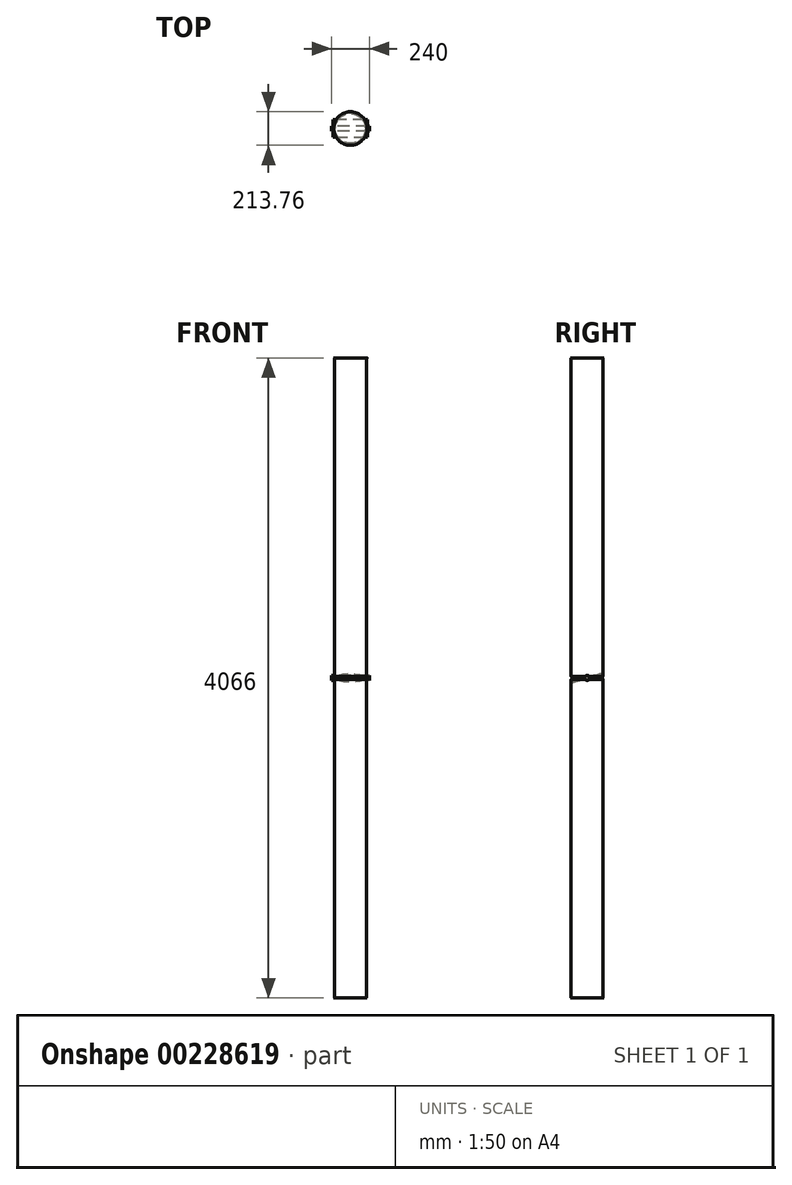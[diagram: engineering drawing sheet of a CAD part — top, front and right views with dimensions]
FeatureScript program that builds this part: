
annotation { "Feature Type Name" : "Feature", "Feature Type Description" : "" }
export const myFeature = defineFeature(function(context is Context, id is Id, definition is map)
    precondition{}
    {
        {
            var Q0;
            Q0=qCreatedBy(makeId("Top.planeOp"),FACE);
            var sketch = newSketch(context, id + "F0", { "sketchPlane" : qUnion([Q0])});
            skCircle(sketch, "E0", {"center": v(0, 0) * mm, "radius": 98 * mm});
            skSolve(sketch);
        }
        {
            var Q0;
            Q0=qSketchRegion(id+"F0",true);
            var Q1;
            Q1=sQuery(id+"F0.wireOp",EDGE,"E0");
            extrude(context, id + "F1", {"entities" : qUnion([Q0]), "surfaceEntities" : qUnion([Q1]), "endBound" : BoundingType.SYMMETRIC, "depth" : 6 * mm});
        }
        {
            var Q0;
            Q0=qCreatedBy(makeId("Top.planeOp"),FACE);
            var sketch = newSketch(context, id + "F2", { "sketchPlane" : qUnion([Q0])});
            skLineSegment(sketch, "E1", {"start": v(-75.72, 0) * mm, "end": v(75.22, 0) * mm});
            skSolve(sketch);
        }
        {
            var Q0;
            Q0=makeQuery(id+"F1.opExtrude","CAP_EDGE",EDGE,{"disambiguationData":[OSD([sQuery(id+"F0.wireOp",EDGE,"E0")])],"isStart":true});
            var Q1;
            Q1=makeQuery(id+"F1.opExtrude","CAP_EDGE",EDGE,{"disambiguationData":[OSD([sQuery(id+"F0.wireOp",EDGE,"E0")])],"isStart":false});
            fillet(context, id + "F3", {"entities" : qUnion([Q0, Q1]), "radius" : 3 * mm, "tangentPropagation" : true, "allowEdgeOverflow" : false});
        }
        {
            var Q0;
            Q0=qCreatedBy(makeId("Top.planeOp"),FACE);
            var sketch = newSketch(context, id + "F4", { "sketchPlane" : qUnion([Q0])});
            skCircle(sketch, "E2", {"center": v(0, 0) * mm, "radius": 101.6 * mm});
            skSolve(sketch);
        }
        {
            var Q0;
            Q0=qSketchRegion(id+"F4",true);
            extrude(context, id + "F5", {"entities" : qUnion([Q0]), "depth" : 2032 * mm, "hasSecondDirection" : true, "secondDirectionOppositeDirection" : true, "secondDirectionDepth" : 2032 * mm});
        }
        {
            var Q0;
            Q0=qCreatedBy(makeId("Right.planeOp"),FACE);
            var sketch = newSketch(context, id + "F6", { "sketchPlane" : qUnion([Q0])});
            skCircle(sketch, "E3", {"center": v(0, 0) * mm, "radius": 16 * mm});
            skSolve(sketch);
        }
        {
            var Q0;
            Q0=qSketchRegion(id+"F6",true);
            extrude(context, id + "F7", {"entities" : qUnion([Q0]), "endBound" : BoundingType.SYMMETRIC, "depth" : 240 * mm});
        }
        {
            var Q0;
            Q0=makeQuery(id+"F4.imprint","IMPRINT",FACE,{"disambiguationData":[TD([[makeQuery(id+"F4.imprint","IMPRINT",EDGE,{"derivedFrom":sQuery(id+"F4.wireOp",EDGE,"E2")}),1.0]])]});
            var Q1;
            Q1=sQuery(id+"F4.wireOp",EDGE,"E2");
            extrude(context, id + "F8", {"entities" : qUnion([Q0]), "surfaceEntities" : qUnion([Q1]), "endBound" : BoundingType.SYMMETRIC, "depth" : 17.2 * mm});
        }
        {
            var Q0;
            Q0=makeQuery(id+"F0.imprint","IMPRINT",FACE,{"disambiguationData":[TD([[makeQuery(id+"F0.imprint","IMPRINT",EDGE,{"derivedFrom":sQuery(id+"F0.wireOp",EDGE,"E0")}),1.0]])]});
            var Q1;
            Q1=sQuery(id+"F0.wireOp",EDGE,"E0");
            extrude(context, id + "F9", {"entities" : qUnion([Q0]), "surfaceEntities" : qUnion([Q1]), "endBound" : BoundingType.SYMMETRIC, "depth" : 50 * mm});
        }
        {
            var Q0;
            Q0=makeQuery(id+"F9.opExtrude","SWEPT_BODY",BODY,{"disambiguationData":[OSD([sQuery(id+"F0.wireOp",EDGE,"E0")])]});
            var Q1;
            Q1=makeQuery(id+"F8.opExtrude","SWEPT_BODY",BODY,{"disambiguationData":[OSD([sQuery(id+"F4.wireOp",EDGE,"E2")])]});
            booleanBodies(context, id + "F10", {"operationType" : BooleanOperationType.SUBTRACTION, "tools" : qUnion([Q0]), "targets" : qUnion([Q1])});
        }
        {
            var Q0;
            Q0=makeQuery(id+"F8.opExtrude","SWEPT_BODY",BODY,{"disambiguationData":[OSD([sQuery(id+"F4.wireOp",EDGE,"E2")])]});
            var Q1;
            Q1=makeQuery(id+"F5.opExtrude","SWEPT_BODY",BODY,{"disambiguationData":[OSD([sQuery(id+"F4.wireOp",EDGE,"E2")])]});
            booleanBodies(context, id + "F11", {"operationType" : BooleanOperationType.SUBTRACTION, "tools" : qUnion([Q0]), "targets" : qUnion([Q1])});
        }
        {
            var Q0;
            Q0=makeQuery(id+"F11.opBoolean","COPY",EDGE,{"derivedFrom":makeQuery(id+"F8.opExtrude","CAP_EDGE",EDGE,{"disambiguationData":[OSD([sQuery(id+"F4.wireOp",EDGE,"E2")])],"isStart":true})});
            var Q1;
            Q1=makeQuery(id+"F11.opBoolean","COPY",EDGE,{"derivedFrom":makeQuery(id+"F10.opBoolean","INTERSECT",EDGE,{"derivedFrom":[makeQuery(id+"F8.opExtrude","CAP_FACE",FACE,{"disambiguationData":[OSD([sQuery(id+"F4.wireOp",EDGE,"E2")])],"isStart":true}),makeQuery(id+"F9.opExtrude","SWEPT_FACE",FACE,{"disambiguationData":[OSD([sQuery(id+"F0.wireOp",EDGE,"E0")])]})]})});
            var Q2;
            Q2=makeQuery(id+"F11.opBoolean","COPY",EDGE,{"derivedFrom":makeQuery(id+"F10.opBoolean","INTERSECT",EDGE,{"derivedFrom":[makeQuery(id+"F8.opExtrude","CAP_FACE",FACE,{"disambiguationData":[OSD([sQuery(id+"F4.wireOp",EDGE,"E2")])],"isStart":false}),makeQuery(id+"F9.opExtrude","SWEPT_FACE",FACE,{"disambiguationData":[OSD([sQuery(id+"F0.wireOp",EDGE,"E0")])]})]})});
            var Q3;
            Q3=makeQuery(id+"F11.opBoolean","COPY",EDGE,{"derivedFrom":makeQuery(id+"F8.opExtrude","CAP_EDGE",EDGE,{"disambiguationData":[OSD([sQuery(id+"F4.wireOp",EDGE,"E2")])],"isStart":false})});
            fillet(context, id + "F12", {"entities" : qUnion([Q0, Q1, Q2, Q3]), "radius" : 1.5 * mm, "tangentPropagation" : true, "allowEdgeOverflow" : false});
        }
        {
            var Q0;
            Q0=qCreatedBy(makeId("Top.planeOp"),FACE);
            var sketch = newSketch(context, id + "F13", { "sketchPlane" : qUnion([Q0])});
            skLineSegment(sketch, "E4.bottom", {"start": v(-110.32, -54.73) * mm, "end": v(109.68, -54.73) * mm});
            skLineSegment(sketch, "E4.top", {"start": v(-110.32, 55.27) * mm, "end": v(109.68, 55.27) * mm});
            skLineSegment(sketch, "E4.left", {"start": v(-110.32, -54.73) * mm, "end": v(-110.32, 55.27) * mm});
            skLineSegment(sketch, "E4.right", {"start": v(109.68, -54.73) * mm, "end": v(109.68, 55.27) * mm});
            skSolve(sketch);
        }
        {
            var Q0;
            Q0=qSketchRegion(id+"F13",true);
            extrude(context, id + "F14", {"entities" : qUnion([Q0]), "endBound" : BoundingType.SYMMETRIC, "depth" : 6 * mm});
        }
        {
            var Q0;
            Q0=makeQuery(id+"F14.opExtrude","CAP_EDGE",EDGE,{"disambiguationData":[OSD([sQuery(id+"F13.wireOp",EDGE,"E4.bottom")])],"isStart":true});
            var Q1;
            Q1=makeQuery(id+"F14.opExtrude","CAP_EDGE",EDGE,{"disambiguationData":[OSD([sQuery(id+"F13.wireOp",EDGE,"E4.bottom")])],"isStart":false});
            var Q2;
            Q2=makeQuery(id+"F14.opExtrude","CAP_EDGE",EDGE,{"disambiguationData":[OSD([sQuery(id+"F13.wireOp",EDGE,"E4.top")])],"isStart":true});
            var Q3;
            Q3=makeQuery(id+"F14.opExtrude","CAP_EDGE",EDGE,{"disambiguationData":[OSD([sQuery(id+"F13.wireOp",EDGE,"E4.top")])],"isStart":false});
            fillet(context, id + "F15", {"entities" : qUnion([Q0, Q1, Q2, Q3]), "radius" : 3 * mm, "tangentPropagation" : true, "allowEdgeOverflow" : false});
        }
        {
            var Q0;
            Q0=makeQuery(id+"F1.opExtrude","SWEPT_BODY",BODY,{"disambiguationData":[OSD([sQuery(id+"F0.wireOp",EDGE,"E0")])]});
            var Q1;
            Q1=sQuery(id+"F2.wireOp",EDGE,"E1");
            transform(context, id + "F16", {"entities" : qUnion([Q0]), "transformType" : TransformType.ROTATION, "transformAxis" : qUnion([Q1]), "angle" : 15 * degree, "makeCopy" : false});
        }
        {
            var Q0;
            Q0=makeQuery(id+"F5.opExtrude","CAP_FACE",FACE,{"disambiguationData":[OSD([sQuery(id+"F4.wireOp",EDGE,"E2")])],"isStart":true});
            var sketch = newSketch(context, id + "F17", { "sketchPlane" : qUnion([Q0])});
            skCircle(sketch, "E5", {"center": v(0, 0) * mm, "radius": 106.52 * mm});
            skSolve(sketch);
        }
        {
            var Q0;
            Q0=makeQuery(id+"F17.imprint","IMPRINT",FACE,{"disambiguationData":[TD([[makeQuery(id+"F17.imprint","IMPRINT",EDGE,{"derivedFrom":makeQuery(id+"F5.opExtrude","CAP_EDGE",EDGE,{"disambiguationData":[OSD([sQuery(id+"F4.wireOp",EDGE,"E2")])],"isStart":true})}),-1.0]])]});
            var Q1;
            Q1=makeQuery(id+"F17.imprint","IMPRINT",FACE,{"disambiguationData":[TD([[makeQuery(id+"F17.imprint","IMPRINT",EDGE,{"derivedFrom":sQuery(id+"F17.wireOp",EDGE,"E5")}),1.0]])]});
            var Q2;
            Q2=sQuery(id+"F17.wireOp",EDGE,"E5");
            extrude(context, id + "F18", {"entities" : qUnion([Q0, Q1]), "surfaceEntities" : qUnion([Q2]), "endBound" : BoundingType.SYMMETRIC, "depth" : 2 * mm});
        }
        {
            var Q0;
            Q0=makeQuery(id+"F5.opExtrude","CAP_FACE",FACE,{"disambiguationData":[OSD([sQuery(id+"F4.wireOp",EDGE,"E2")])],"isStart":false});
            var sketch = newSketch(context, id + "F19", { "sketchPlane" : qUnion([Q0])});
            skCircle(sketch, "E6", {"center": v(0, 0) * mm, "radius": 106.88 * mm});
            skSolve(sketch);
        }
        {
            var Q0;
            Q0=makeQuery(id+"F19.imprint","IMPRINT",FACE,{"disambiguationData":[TD([[makeQuery(id+"F19.imprint","IMPRINT",EDGE,{"derivedFrom":makeQuery(id+"F5.opExtrude","CAP_EDGE",EDGE,{"disambiguationData":[OSD([sQuery(id+"F4.wireOp",EDGE,"E2")])],"isStart":false})}),1.0]])]});
            var Q1;
            Q1=makeQuery(id+"F19.imprint","IMPRINT",FACE,{"disambiguationData":[TD([[makeQuery(id+"F19.imprint","IMPRINT",EDGE,{"derivedFrom":sQuery(id+"F19.wireOp",EDGE,"E6")}),1.0]])]});
            extrude(context, id + "F20", {"entities" : qUnion([Q0, Q1]), "endBound" : BoundingType.SYMMETRIC, "depth" : 2 * mm});
        }
    });
